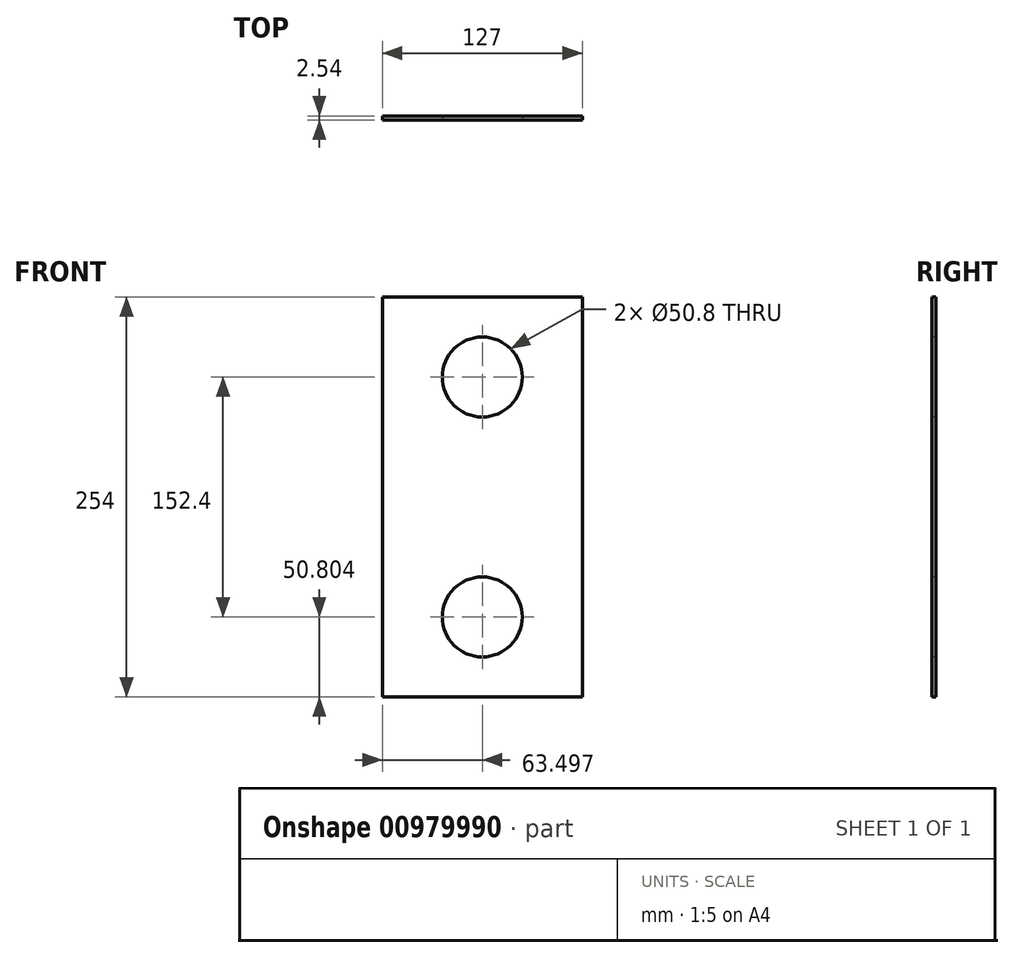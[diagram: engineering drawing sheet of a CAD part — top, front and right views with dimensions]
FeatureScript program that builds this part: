
annotation { "Feature Type Name" : "Feature", "Feature Type Description" : "" }
export const myFeature = defineFeature(function(context is Context, id is Id, definition is map)
    precondition{}
    {
        {
            var Q0;
            Q0=qCreatedBy(makeId("Front.planeOp"),FACE);
            var sketch = newSketch(context, id + "F0", { "sketchPlane" : qUnion([Q0])});
            skLineSegment(sketch, "E0.bottom", {"start": v(-155.48, 257.96) * mm, "end": v(-28.48, 257.96) * mm});
            skLineSegment(sketch, "E0.top", {"start": v(-155.48, 3.96) * mm, "end": v(-28.48, 3.96) * mm});
            skLineSegment(sketch, "E0.left", {"start": v(-155.48, 257.96) * mm, "end": v(-155.48, 3.96) * mm});
            skLineSegment(sketch, "E0.right", {"start": v(-28.48, 257.96) * mm, "end": v(-28.48, 3.96) * mm});
            skSolve(sketch);
        }
        {
            var Q0;
            Q0=makeQuery(id+"F0.imprint","IMPRINT",FACE,{"disambiguationData":[TD([[makeQuery(id+"F0.imprint","IMPRINT",EDGE,{"derivedFrom":sQuery(id+"F0.wireOp",EDGE,"E0.bottom")}),-1.0]])]});
            extrude(context, id + "F1", {"entities" : qUnion([Q0]), "depth" : 2.54 * mm, "offsetDistance" : 25.4 * mm});
        }
        {
            var Q0;
            Q0=makeQuery(id+"F1.opExtrude","CAP_FACE",FACE,{"disambiguationData":[OSD([sQuery(id+"F0.wireOp",EDGE,"E0.bottom"),sQuery(id+"F0.wireOp",EDGE,"E0.top"),sQuery(id+"F0.wireOp",EDGE,"E0.left"),sQuery(id+"F0.wireOp",EDGE,"E0.right")])],"isStart":false});
            var sketch = newSketch(context, id + "F2", { "sketchPlane" : qUnion([Q0])});
            skLineSegment(sketch, "E1.bottom", {"start": v(-155.48, 257.96) * mm, "end": v(-28.48, 257.96) * mm});
            skLineSegment(sketch, "E1.top", {"start": v(-155.48, 232.56) * mm, "end": v(-28.48, 232.56) * mm});
            skLineSegment(sketch, "E1.left", {"start": v(-155.48, 257.96) * mm, "end": v(-155.48, 232.56) * mm});
            skLineSegment(sketch, "E1.right", {"start": v(-28.48, 257.96) * mm, "end": v(-28.48, 232.56) * mm});
            skLineSegment(sketch, "E2.top", {"start": v(-155.48, 181.76) * mm, "end": v(-28.48, 181.76) * mm});
            skLineSegment(sketch, "E2.left", {"start": v(-155.48, 232.56) * mm, "end": v(-155.48, 181.76) * mm});
            skLineSegment(sketch, "E2.right", {"start": v(-28.48, 232.56) * mm, "end": v(-28.48, 181.76) * mm});
            skLineSegment(sketch, "E3", {"start": v(-91.98, 232.56) * mm, "end": v(-91.98, 181.76) * mm});
            skCircle(sketch, "E4", {"center": v(-91.98, 207.16) * mm, "radius": 25.4 * mm});
            skSolve(sketch);
        }
        {
            var Q0;
            {var subQ0=sQuery(id+"F2.wireOp",EDGE,"E3");Q0=makeQuery(id+"F2.imprint","IMPRINT",FACE,{"disambiguationData":[TD([[makeQuery(id+"F2.imprint","IMPRINT",EDGE,{"derivedFrom":subQ0}),-1.0]])]});}
            var Q1;
            {var subQ0=sQuery(id+"F2.wireOp",EDGE,"E3");Q1=makeQuery(id+"F2.imprint","IMPRINT",FACE,{"disambiguationData":[TD([[makeQuery(id+"F2.imprint","IMPRINT",EDGE,{"derivedFrom":subQ0}),1.0]])]});}
            extrude(context, id + "F3", {"entities" : qUnion([Q0, Q1]), "operationType" : NewBodyOperationType.REMOVE, "oppositeDirection" : true, "depth" : 25.4 * mm, "offsetDistance" : 25.4 * mm});
        }
        {
            var Q0;
            Q0=makeQuery(id+"F1.opExtrude","CAP_FACE",FACE,{"disambiguationData":[OSD([sQuery(id+"F0.wireOp",EDGE,"E0.bottom"),sQuery(id+"F0.wireOp",EDGE,"E0.top"),sQuery(id+"F0.wireOp",EDGE,"E0.left"),sQuery(id+"F0.wireOp",EDGE,"E0.right")])],"isStart":false});
            var sketch = newSketch(context, id + "F4", { "sketchPlane" : qUnion([Q0])});
            skLineSegment(sketch, "E5.bottom", {"start": v(-155.48, 3.96) * mm, "end": v(-28.48, 3.96) * mm});
            skLineSegment(sketch, "E5.top", {"start": v(-155.48, 29.36) * mm, "end": v(-28.48, 29.36) * mm});
            skLineSegment(sketch, "E5.left", {"start": v(-155.48, 3.96) * mm, "end": v(-155.48, 29.36) * mm});
            skLineSegment(sketch, "E5.right", {"start": v(-28.48, 3.96) * mm, "end": v(-28.48, 29.36) * mm});
            skLineSegment(sketch, "E6.top", {"start": v(-155.48, 80.16) * mm, "end": v(-28.48, 80.16) * mm});
            skLineSegment(sketch, "E6.left", {"start": v(-155.48, 29.36) * mm, "end": v(-155.48, 80.16) * mm});
            skLineSegment(sketch, "E6.right", {"start": v(-28.48, 29.36) * mm, "end": v(-28.48, 80.16) * mm});
            skLineSegment(sketch, "E7", {"start": v(-155.48, 80.16) * mm, "end": v(-91.98, 80.16) * mm});
            skLineSegment(sketch, "E8", {"start": v(-91.98, 80.16) * mm, "end": v(-91.98, 29.36) * mm});
            skCircle(sketch, "E9", {"center": v(-91.98, 54.76) * mm, "radius": 25.4 * mm});
            skSolve(sketch);
        }
        {
            var Q0;
            {var subQ0=sQuery(id+"F4.wireOp",EDGE,"E8");Q0=makeQuery(id+"F4.imprint","IMPRINT",FACE,{"disambiguationData":[TD([[makeQuery(id+"F4.imprint","IMPRINT",EDGE,{"derivedFrom":subQ0}),-1.0]])]});}
            var Q1;
            {var subQ0=sQuery(id+"F4.wireOp",EDGE,"E8");Q1=makeQuery(id+"F4.imprint","IMPRINT",FACE,{"disambiguationData":[TD([[makeQuery(id+"F4.imprint","IMPRINT",EDGE,{"derivedFrom":subQ0}),1.0]])]});}
            extrude(context, id + "F5", {"entities" : qUnion([Q0, Q1]), "operationType" : NewBodyOperationType.REMOVE, "oppositeDirection" : true, "depth" : 25.4 * mm, "offsetDistance" : 25.4 * mm});
        }
    });
